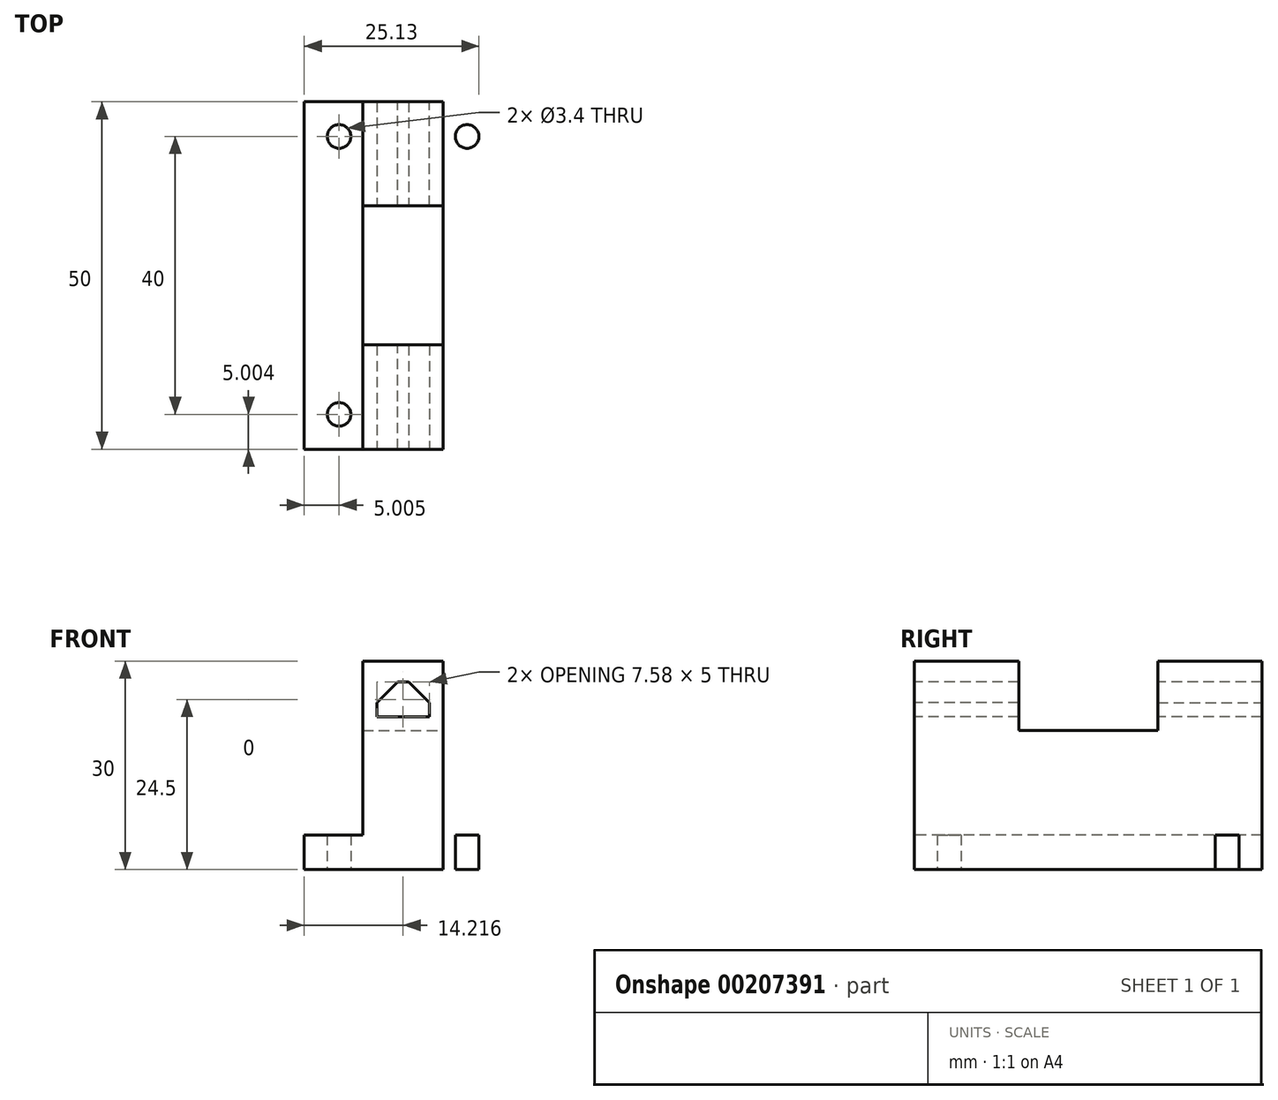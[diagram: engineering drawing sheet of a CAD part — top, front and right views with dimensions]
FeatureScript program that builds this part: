
annotation { "Feature Type Name" : "Feature", "Feature Type Description" : "" }
export const myFeature = defineFeature(function(context is Context, id is Id, definition is map)
    precondition{}
    {
        {
            var Q0;
            Q0=qCreatedBy(makeId("Top.planeOp"),FACE);
            var sketch = newSketch(context, id + "F0", { "sketchPlane" : qUnion([Q0])});
            skCircle(sketch, "E0", {"center": v(26.44, -27.59) * mm, "radius": 1.7 * mm});
            skLineSegment(sketch, "E1", {"start": v(21.44, -22.59) * mm, "end": v(21.44, -47.59) * mm});
            skLineSegment(sketch, "E2.left", {"start": v(29.87, -22.59) * mm, "end": v(29.87, -37.59) * mm});
            skLineSegment(sketch, "E3", {"start": v(21.44, -22.59) * mm, "end": v(35.66, -22.59) * mm});
            skLineSegment(sketch, "E4", {"start": v(21.44, -47.59) * mm, "end": v(35.66, -47.59) * mm, "construction": true});
            skLineSegment(sketch, "E5", {"start": v(29.87, -37.59) * mm, "end": v(35.66, -37.59) * mm});
            skLineSegment(sketch, "E6", {"start": v(35.66, -47.59) * mm, "end": v(35.66, -22.59) * mm, "construction": true});
            skCircle(sketch, "E7.0.MirrorC", {"center": v(44.87, -27.59) * mm, "radius": 1.7 * mm});
            skLineSegment(sketch, "E7.1.MirrorCS", {"start": v(41.45, -22.59) * mm, "end": v(41.45, -37.59) * mm});
            skLineSegment(sketch, "E8.0.MirrorCS", {"start": v(49.87, -22.59) * mm, "end": v(35.66, -22.59) * mm});
            skLineSegment(sketch, "E9.0.MirrorCS", {"start": v(49.87, -22.59) * mm, "end": v(49.87, -47.59) * mm});
            skLineSegment(sketch, "E10.0.MirrorCS", {"start": v(49.87, -47.59) * mm, "end": v(35.66, -47.59) * mm, "construction": true});
            skLineSegment(sketch, "E11.0.MirrorCS", {"start": v(41.45, -37.59) * mm, "end": v(35.66, -37.59) * mm});
            skLineSegment(sketch, "E12.0.MirrorCS", {"start": v(21.44, -72.59) * mm, "end": v(21.44, -47.59) * mm});
            skLineSegment(sketch, "E13.0.MirrorCS", {"start": v(49.87, -72.59) * mm, "end": v(49.87, -47.59) * mm});
            skLineSegment(sketch, "E14.0.MirrorCS", {"start": v(35.66, -47.59) * mm, "end": v(35.66, -72.59) * mm, "construction": true});
            skLineSegment(sketch, "E14.1.MirrorCS", {"start": v(29.87, -57.59) * mm, "end": v(35.66, -57.59) * mm});
            skLineSegment(sketch, "E14.2.MirrorCS", {"start": v(49.87, -72.59) * mm, "end": v(35.66, -72.59) * mm});
            skCircle(sketch, "E14.4.MirrorC", {"center": v(44.87, -67.59) * mm, "radius": 1.7 * mm});
            skCircle(sketch, "E14.5.MirrorC", {"center": v(26.44, -67.59) * mm, "radius": 1.7 * mm});
            skLineSegment(sketch, "E14.6.MirrorCS", {"start": v(41.45, -72.59) * mm, "end": v(41.45, -57.59) * mm});
            skLineSegment(sketch, "E14.7.MirrorCS", {"start": v(41.45, -57.59) * mm, "end": v(35.66, -57.59) * mm});
            skLineSegment(sketch, "E14.8.MirrorCS", {"start": v(21.44, -72.59) * mm, "end": v(35.66, -72.59) * mm});
            skLineSegment(sketch, "E14.10.MirrorCS", {"start": v(29.87, -72.59) * mm, "end": v(29.87, -57.59) * mm});
            skLineSegment(sketch, "E15", {"start": v(29.87, -37.59) * mm, "end": v(29.87, -47.59) * mm});
            skLineSegment(sketch, "E16.0.MirrorCS", {"start": v(41.45, -37.59) * mm, "end": v(41.45, -47.59) * mm});
            skLineSegment(sketch, "E17.0.MirrorCS", {"start": v(29.87, -57.59) * mm, "end": v(29.87, -47.59) * mm});
            skLineSegment(sketch, "E18.0.MirrorCS", {"start": v(41.45, -57.59) * mm, "end": v(41.45, -47.59) * mm});
            skSolve(sketch);
        }
        {
            var Q0;
            Q0=makeQuery(id+"F0.imprint","IMPRINT",FACE,{"disambiguationData":[TD([[makeQuery(id+"F0.imprint","IMPRINT",EDGE,{"derivedFrom":sQuery(id+"F0.wireOp",EDGE,"E0")}),-1.0]])]});
            var Q1;
            Q1=makeQuery(id+"F0.imprint","IMPRINT",FACE,{"disambiguationData":[TD([[makeQuery(id+"F0.imprint","IMPRINT",EDGE,{"derivedFrom":sQuery(id+"F0.wireOp",EDGE,"E7.0.MirrorC")}),1.0]])]});
            extrude(context, id + "F1", {"entities" : qUnion([Q0, Q1]), "depth" : 5 * mm});
        }
        {
            var Q0;
            {var subQ4=sQuery(id+"F0.wireOp",EDGE,"E2.left");Q0=makeQuery(id+"F0.imprint","IMPRINT",FACE,{"disambiguationData":[TD([[makeQuery(id+"F0.imprint","IMPRINT",EDGE,{"derivedFrom":subQ4}),1.0]])]});}
            var Q1;
            Q1=makeQuery(id+"F0.imprint","IMPRINT",FACE,{"disambiguationData":[TD([[makeQuery(id+"F0.imprint","IMPRINT",EDGE,{"derivedFrom":sQuery(id+"F0.wireOp",EDGE,"E14.1.MirrorCS")}),-1.0]])]});
            extrude(context, id + "F2", {"entities" : qUnion([Q0, Q1]), "operationType" : NewBodyOperationType.ADD, "depth" : 30 * mm});
        }
        {
            var Q0;
            Q0=makeQuery(id+"F0.imprint","IMPRINT",FACE,{"disambiguationData":[TD([[makeQuery(id+"F0.imprint","IMPRINT",EDGE,{"derivedFrom":sQuery(id+"F0.wireOp",EDGE,"E5")}),-1.0]])]});
            extrude(context, id + "F3", {"entities" : qUnion([Q0]), "operationType" : NewBodyOperationType.ADD, "depth" : 20 * mm});
        }
        {
            var Q0;
            {var subQ0=sQuery(id+"F0.wireOp",EDGE,"E14.2.MirrorCS");var subQ1=sQuery(id+"F0.wireOp",EDGE,"E14.8.MirrorCS");Q0=makeQuery(id+"F2.boolean.opBoolean","MERGE",FACE,{"derivedFrom":[makeQuery(id+"F1.opExtrude","SWEPT_FACE",FACE,{"disambiguationData":[OSD([subQ0])]}),makeQuery(id+"F1.opExtrude","SWEPT_FACE",FACE,{"disambiguationData":[OSD([subQ1])]}),makeQuery(id+"F2.opExtrude","SWEPT_FACE",FACE,{"disambiguationData":[OSD([subQ0,subQ1])]})]});}
            var sketch = newSketch(context, id + "F4", { "sketchPlane" : qUnion([Q0])});
            skLineSegment(sketch, "E19.bottom", {"start": v(31.87, 27) * mm, "end": v(39.45, 27) * mm});
            skLineSegment(sketch, "E19.top", {"start": v(31.87, 22) * mm, "end": v(39.45, 22) * mm});
            skLineSegment(sketch, "E19.left", {"start": v(31.87, 27) * mm, "end": v(31.87, 22) * mm});
            skLineSegment(sketch, "E19.right", {"start": v(39.45, 27) * mm, "end": v(39.45, 22) * mm});
            skSolve(sketch);
        }
        {
            var Q0;
            Q0=makeQuery(id+"F4.imprint","IMPRINT",FACE,{"disambiguationData":[TD([[makeQuery(id+"F4.imprint","IMPRINT",EDGE,{"derivedFrom":sQuery(id+"F4.wireOp",EDGE,"E19.bottom")}),-1.0]])]});
            extrude(context, id + "F5", {"entities" : qUnion([Q0]), "operationType" : NewBodyOperationType.REMOVE, "endBound" : BoundingType.THROUGH_ALL, "oppositeDirection" : true, "depth" : 25 * mm});
        }
        {
            var Q0;
            Q0=makeQuery(id+"F5.boolean.opBoolean","COPY",EDGE,{"disambiguationData":[OD(0.0)],"derivedFrom":makeQuery(id+"F5.opExtrude","SWEPT_EDGE",EDGE,{"disambiguationData":[OSD([sQuery(id+"F4.wireOp",EDGE,"E19.bottom"),sQuery(id+"F4.wireOp",EDGE,"E19.left")])]})});
            var Q1;
            Q1=makeQuery(id+"F5.boolean.opBoolean","COPY",EDGE,{"disambiguationData":[OD(0.0)],"derivedFrom":makeQuery(id+"F5.opExtrude","SWEPT_EDGE",EDGE,{"disambiguationData":[OSD([sQuery(id+"F4.wireOp",EDGE,"E19.bottom"),sQuery(id+"F4.wireOp",EDGE,"E19.right")])]})});
            var Q2;
            Q2=makeQuery(id+"F5.boolean.opBoolean","COPY",EDGE,{"disambiguationData":[OD(1.0)],"derivedFrom":makeQuery(id+"F5.opExtrude","SWEPT_EDGE",EDGE,{"disambiguationData":[OSD([sQuery(id+"F4.wireOp",EDGE,"E19.bottom"),sQuery(id+"F4.wireOp",EDGE,"E19.left")])]})});
            var Q3;
            Q3=makeQuery(id+"F5.boolean.opBoolean","COPY",EDGE,{"disambiguationData":[OD(1.0)],"derivedFrom":makeQuery(id+"F5.opExtrude","SWEPT_EDGE",EDGE,{"disambiguationData":[OSD([sQuery(id+"F4.wireOp",EDGE,"E19.bottom"),sQuery(id+"F4.wireOp",EDGE,"E19.right")])]})});
            chamfer(context, id + "F6", {"entities" : qUnion([Q0, Q1, Q2, Q3]), "width" : 3 * mm, "tangentPropagation" : true});
        }
    });
